# Revit family: Access_Door-Draft_Stop-Cendrex-Attic_Application-DRD
name_source: partatom
category: Specialty Equipment
revit_build: Autodesk Revit Architecture 2013 (Build: 20130531_2115(x64)
units: mm (PartAtom-declared; Revit-internal decimal feet)

## types (9) — shared parameters
Assembly Code = C1020700
Available Options = http://cendrex.com
Cendrex LEED Ready Program = http://www.cendrex.com
Construction Material = Metal - Cendrex - Aluminum
Default Elevation = 0"
Description = Draft stop access door for attic application
Finish = Metal - Cendrex - Powder Coated White
Frame Depth = 2 1/2"
Manufacturer = Cendrex
Model = DRD
Product Documentation Link = http://cendrex.com
Product Page URL = http://cendrex.com
URL = http://www.cendrex.com

## per-type parameters (varying)
| type | Door Height Calc | Door Width Calc | Frame Height | Frame Width | Height | Width |
| 22 x 30 | 30" | 22" | 32 1/4" | 24 1/4" | 30" | 22" |
| 22 x 36 | 36" | 22" | 38 1/4" | 24 1/4" | 36" | 22" |
| 24 x 36 | 36" | 24" | 38 1/4" | 26 1/4" | 36" | 24" |
| 24 x 48 | 48" | 24" | 50 1/4" | 26 1/4" | 48" | 24" |
| 24 x 60 | 60" | 24" | 62 1/4" | 26 1/4" | 60" | 24" |
| 30 x 30 | 30" | 30" | 32 1/4" | 32 1/4" | 30" | 30" |
| 36 x 36 | 36" | 36" | 38 1/4" | 38 1/4" | 36" | 36" |
| 36 x 48 | 48" | 36" | 50 1/4" | 38 1/4" | 48" | 36" |
| Custom | 24" | 24" | 26 1/4" | 26 1/4" | 24" | 24" |

## geometry (parser evidence)
native form markers: Blend x8, Sweep x9
no freeform markers — native parametric forms only
